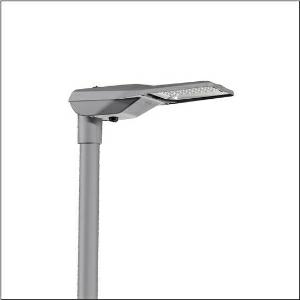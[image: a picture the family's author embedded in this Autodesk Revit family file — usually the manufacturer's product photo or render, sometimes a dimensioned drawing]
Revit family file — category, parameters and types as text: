
# Revit family: streetlight_sl_21_mini___st0_5a_5xe2b33t08gb_0718
name_source: partatom
category: Lighting Fixtures
units: mm (PartAtom-declared; Revit-internal decimal feet)

## family parameters
Cut with Voids When Loaded = No
Host = Face
Light Source = No
Part Type = Normal
Room Calculation Point = No
Round Connector Dimension = Use Diameter
Shared = No

## types (1)
- --- (1 x LED, 5940 lm, 40.4 W, 3000K)
    Apparent Load = 40 VA
    CIE Flux Codes = 41 75 97 100 100
    Color Rendering = 70
    Color Temperature = 3000K
    Default Elevation = 1800 mm
    Description = Streetlight SL 21 mini, mast luminaire, primary light control with lens, of PMMA, primary optical cover: cover, of toughened safety glass, transparent, light distribution: ST0.5a, light emission: direct distribution, primary light characteristic: asymmetric, installation type: side-entry, post-top, LED, High Power LED, rated luminous flux: 5.940lm, luminous efficacy: 147lm/W, light colour: 730, colour temperature: 3000K, control gear: D4i, control: overheat protection, constant luminous flux control, time-dependent luminous flux control, flexible luminous flux parameterisation, pre-setting: logarithmic dimming characteristic, mains connection: 220..240V, AC, 50/60Hz, start of lifetime: 40W, end of service life: 41W, reduction: 19W, luminaire housing, of diecast aluminium, powder-coated, Siteco® metallic grey (DB 702S), corrosivity category C5 mid according to DIN EN ISO 12944, please order mast flange separately, inclination adjustable: 0°, 5°, 10°, 15°, sealing non-destructively replaceable, multi-level sealing system, length: 628mm, width: 235mm, height: 110mm, mast flange for spigot size: 42mm (side-entry): 5XC10008XM4, 60/48mm (side-entry/post-top): 5XC10108XM2, 76/60mm (side-entry/post-top): 5XC10108XM1, mounting height: 4..8m, Smart Interface below and above, protection rating (complete): IP66, insulation class (complete): insulation class II (safety insulation), certification: CE, ENEC, ENEC+, VDE, impact resistance: IK10, permissible operating ambient temperature for outdoor applications: -40..+50°C, standard-compliant lighting for roads and squares, packaging unit: 1 piece

Light Distribution: ST0.5a
    Height = 110 mm
    Lamp = 1 x LED
    Lamp Light Flux = 5940 lm
    Lamp Power = 40.4 W
    Lamp count = 1
    Length = 625 mm
    Luminous efficacy = 147 lm/W
    Manufacturer = Siteco
    ModVariant = No
    Model = 5XE2B33T08GB
    Number of Poles = 1
    OnlyDefault = Yes
    Power Factor = 1
    Product Name = Streetlight SL 21 mini | ST0.5a
    Product group = mast luminaire | pylon top
    ProductGroupID = 6100
    Protection Class = Protection class II
    Protection Degree = IP 66
    RLX_Detail_Level = 1
    RLX_Emergency_Light_Flux = 0 lm
    RLX_Emergency_Type = 0
    RLX_Emergency_Type_DB = No
    RlxData = <blob elided: 37369 chars, md5=693612ae>
    Socket = socket
    Standby Power = 0 W
    System Light Flux = 5940 lm
    System Power = 40 W
    Type Comments = factory setting: luminous flux: 100 % | dim-lin: 254 | 812 mA
    Type Image = l_1003514.jpg
    URL = http://relux.com
    VarID = @adj_212413
    Voltage = 0 V
    Weight = 0.00 kg
    Width = 234 mm

## geometry (parser evidence)
native form markers: Blend x4, Sweep x12
no freeform markers — native parametric forms only
